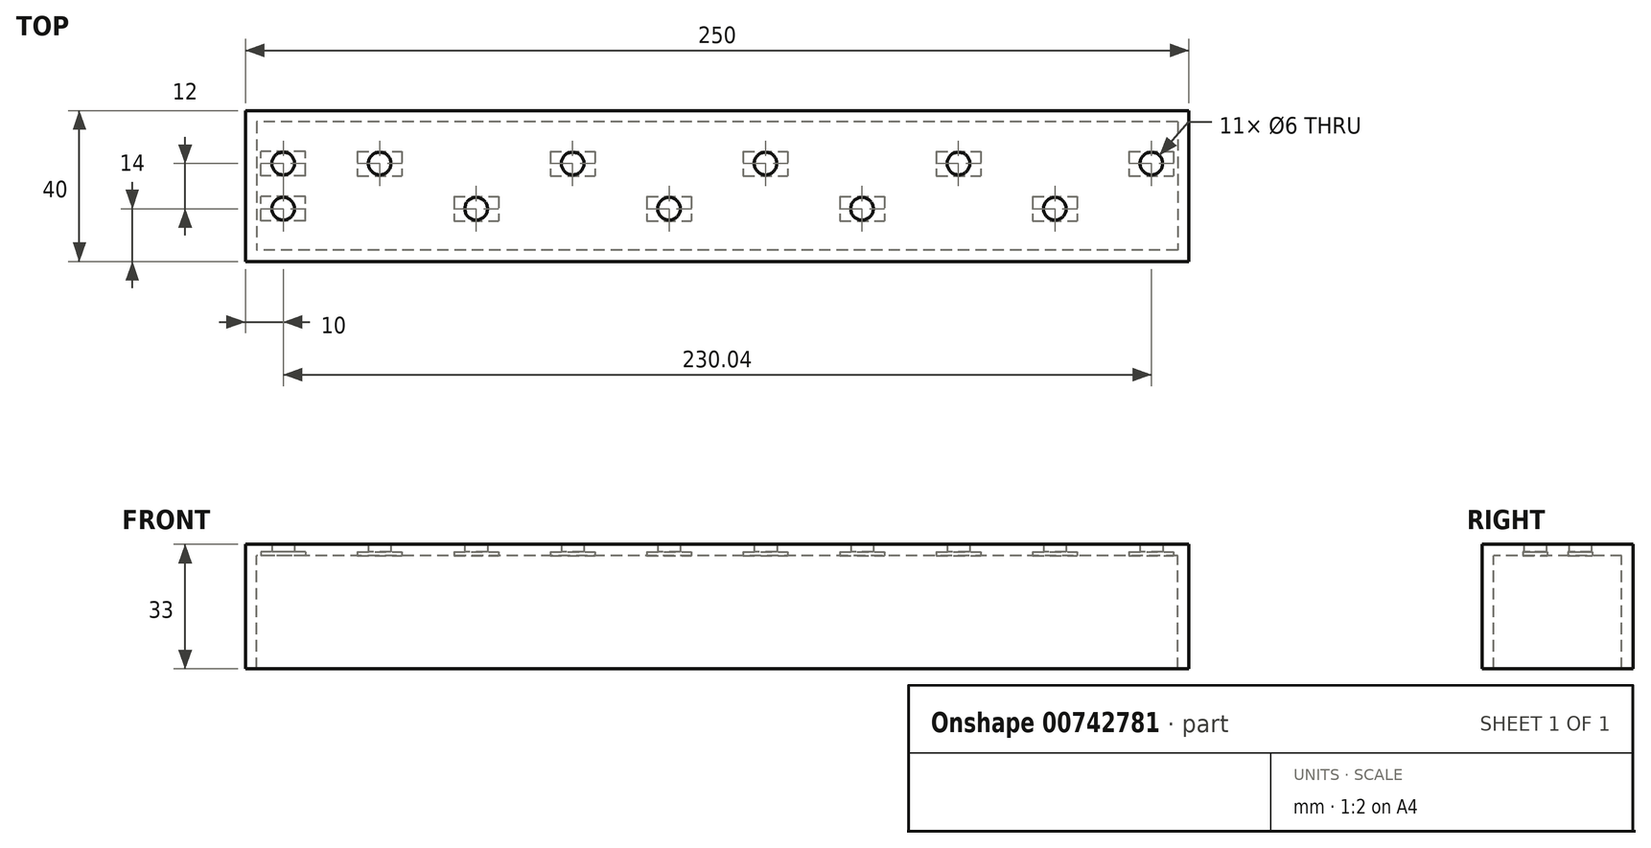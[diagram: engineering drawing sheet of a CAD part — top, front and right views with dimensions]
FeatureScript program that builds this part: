
annotation { "Feature Type Name" : "Feature", "Feature Type Description" : "" }
export const myFeature = defineFeature(function(context is Context, id is Id, definition is map)
    precondition{}
    {
        {
            var Q0;
            Q0=qCreatedBy(makeId("Top.planeOp"),FACE);
            var sketch = newSketch(context, id + "F0", { "sketchPlane" : qUnion([Q0])});
            skLineSegment(sketch, "E0.bottom", {"start": v(125, 20) * mm, "end": v(-125, 20) * mm});
            skLineSegment(sketch, "E0.top", {"start": v(125, -20) * mm, "end": v(-125, -20) * mm});
            skLineSegment(sketch, "E0.left", {"start": v(125, 20) * mm, "end": v(125, -20) * mm});
            skLineSegment(sketch, "E0.right", {"start": v(-125, 20) * mm, "end": v(-125, -20) * mm});
            skPoint(sketch, "E0.middle", {"position": v(0, 0) * mm});
            skLineSegment(sketch, "E1.bottom", {"start": v(115, 6) * mm, "end": v(-115, 6) * mm});
            skLineSegment(sketch, "E1.top", {"start": v(115, -6) * mm, "end": v(-115, -6) * mm});
            skLineSegment(sketch, "E1.left", {"start": v(115, 6) * mm, "end": v(115, -6) * mm});
            skLineSegment(sketch, "E1.right", {"start": v(-115, 6) * mm, "end": v(-115, -6) * mm});
            skCircle(sketch, "E2", {"center": v(-115, -6) * mm, "radius": 3 * mm});
            skLineSegment(sketch, "E3.bottom", {"start": v(-109.1, -9.25) * mm, "end": v(-109.1, -2.75) * mm});
            skLineSegment(sketch, "E3.top", {"start": v(-120.9, -9.25) * mm, "end": v(-120.9, -2.75) * mm});
            skLineSegment(sketch, "E3.left", {"start": v(-109.1, -9.25) * mm, "end": v(-120.9, -9.25) * mm});
            skLineSegment(sketch, "E3.right", {"start": v(-109.1, -2.75) * mm, "end": v(-120.9, -2.75) * mm});
            skCircle(sketch, "E4.0.1.0", {"center": v(-115, 6) * mm, "radius": 3 * mm});
            skPoint(sketch, "E4.0.1.1", {"position": v(-115, 6) * mm});
            skLineSegment(sketch, "E4.0.1.2", {"start": v(-109.1, 2.75) * mm, "end": v(-109.1, 9.25) * mm});
            skLineSegment(sketch, "E4.0.1.3", {"start": v(-120.9, 2.75) * mm, "end": v(-120.9, 9.25) * mm});
            skLineSegment(sketch, "E4.0.1.4", {"start": v(-109.1, 2.75) * mm, "end": v(-120.9, 2.75) * mm});
            skLineSegment(sketch, "E4.0.1.5", {"start": v(-109.1, 9.25) * mm, "end": v(-120.9, 9.25) * mm});
            skCircle(sketch, "E4.1.1.0", {"center": v(-89.44, 6) * mm, "radius": 3 * mm});
            skPoint(sketch, "E4.1.1.1", {"position": v(-89.44, 6) * mm});
            skLineSegment(sketch, "E4.1.1.2", {"start": v(-95.34, 9.25) * mm, "end": v(-95.34, 2.75) * mm});
            skLineSegment(sketch, "E4.1.1.3", {"start": v(-83.54, 9.25) * mm, "end": v(-83.54, 2.75) * mm});
            skLineSegment(sketch, "E4.1.1.4", {"start": v(-95.34, 9.25) * mm, "end": v(-83.54, 9.25) * mm});
            skLineSegment(sketch, "E4.1.1.5", {"start": v(-95.34, 2.75) * mm, "end": v(-83.54, 2.75) * mm});
            skCircle(sketch, "E4.2.0.0", {"center": v(-63.88, -6) * mm, "radius": 3 * mm});
            skPoint(sketch, "E4.2.0.1", {"position": v(-63.88, -6) * mm});
            skLineSegment(sketch, "E4.2.0.2", {"start": v(-69.78, -2.75) * mm, "end": v(-69.78, -9.25) * mm});
            skLineSegment(sketch, "E4.2.0.3", {"start": v(-57.98, -2.75) * mm, "end": v(-57.98, -9.25) * mm});
            skLineSegment(sketch, "E4.2.0.4", {"start": v(-69.78, -2.75) * mm, "end": v(-57.98, -2.75) * mm});
            skLineSegment(sketch, "E4.2.0.5", {"start": v(-69.78, -9.25) * mm, "end": v(-57.98, -9.25) * mm});
            skCircle(sketch, "E4.3.1.0", {"center": v(-38.32, 6) * mm, "radius": 3 * mm});
            skPoint(sketch, "E4.3.1.1", {"position": v(-38.32, 6) * mm});
            skLineSegment(sketch, "E4.3.1.2", {"start": v(-44.22, 9.25) * mm, "end": v(-44.22, 2.75) * mm});
            skLineSegment(sketch, "E4.3.1.3", {"start": v(-32.42, 9.25) * mm, "end": v(-32.42, 2.75) * mm});
            skLineSegment(sketch, "E4.3.1.4", {"start": v(-44.22, 9.25) * mm, "end": v(-32.42, 9.25) * mm});
            skLineSegment(sketch, "E4.3.1.5", {"start": v(-44.22, 2.75) * mm, "end": v(-32.42, 2.75) * mm});
            skCircle(sketch, "E4.4.0.0", {"center": v(-12.76, -6) * mm, "radius": 3 * mm});
            skPoint(sketch, "E4.4.0.1", {"position": v(-12.76, -6) * mm});
            skLineSegment(sketch, "E4.4.0.2", {"start": v(-18.66, -2.75) * mm, "end": v(-18.66, -9.25) * mm});
            skLineSegment(sketch, "E4.4.0.3", {"start": v(-6.86, -2.75) * mm, "end": v(-6.86, -9.25) * mm});
            skLineSegment(sketch, "E4.4.0.4", {"start": v(-18.66, -2.75) * mm, "end": v(-6.86, -2.75) * mm});
            skLineSegment(sketch, "E4.4.0.5", {"start": v(-18.66, -9.25) * mm, "end": v(-6.86, -9.25) * mm});
            skCircle(sketch, "E4.5.1.0", {"center": v(12.8, 6) * mm, "radius": 3 * mm});
            skPoint(sketch, "E4.5.1.1", {"position": v(12.8, 6) * mm});
            skLineSegment(sketch, "E4.5.1.2", {"start": v(6.9, 9.25) * mm, "end": v(6.9, 2.75) * mm});
            skLineSegment(sketch, "E4.5.1.3", {"start": v(18.7, 9.25) * mm, "end": v(18.7, 2.75) * mm});
            skLineSegment(sketch, "E4.5.1.4", {"start": v(6.9, 9.25) * mm, "end": v(18.7, 9.25) * mm});
            skLineSegment(sketch, "E4.5.1.5", {"start": v(6.9, 2.75) * mm, "end": v(18.7, 2.75) * mm});
            skCircle(sketch, "E4.6.0.0", {"center": v(38.36, -6) * mm, "radius": 3 * mm});
            skPoint(sketch, "E4.6.0.1", {"position": v(38.36, -6) * mm});
            skLineSegment(sketch, "E4.6.0.2", {"start": v(32.46, -2.75) * mm, "end": v(32.46, -9.25) * mm});
            skLineSegment(sketch, "E4.6.0.3", {"start": v(44.26, -2.75) * mm, "end": v(44.26, -9.25) * mm});
            skLineSegment(sketch, "E4.6.0.4", {"start": v(32.46, -2.75) * mm, "end": v(44.26, -2.75) * mm});
            skLineSegment(sketch, "E4.6.0.5", {"start": v(32.46, -9.25) * mm, "end": v(44.26, -9.25) * mm});
            skCircle(sketch, "E4.7.1.0", {"center": v(63.92, 6) * mm, "radius": 3 * mm});
            skPoint(sketch, "E4.7.1.1", {"position": v(63.92, 6) * mm});
            skLineSegment(sketch, "E4.7.1.2", {"start": v(58.02, 9.25) * mm, "end": v(58.02, 2.75) * mm});
            skLineSegment(sketch, "E4.7.1.3", {"start": v(69.82, 9.25) * mm, "end": v(69.82, 2.75) * mm});
            skLineSegment(sketch, "E4.7.1.4", {"start": v(58.02, 9.25) * mm, "end": v(69.82, 9.25) * mm});
            skLineSegment(sketch, "E4.7.1.5", {"start": v(58.02, 2.75) * mm, "end": v(69.82, 2.75) * mm});
            skCircle(sketch, "E4.8.0.0", {"center": v(89.48, -6) * mm, "radius": 3 * mm});
            skPoint(sketch, "E4.8.0.1", {"position": v(89.48, -6) * mm});
            skLineSegment(sketch, "E4.8.0.2", {"start": v(83.58, -2.75) * mm, "end": v(83.58, -9.25) * mm});
            skLineSegment(sketch, "E4.8.0.3", {"start": v(95.38, -2.75) * mm, "end": v(95.38, -9.25) * mm});
            skLineSegment(sketch, "E4.8.0.4", {"start": v(83.58, -2.75) * mm, "end": v(95.38, -2.75) * mm});
            skLineSegment(sketch, "E4.8.0.5", {"start": v(83.58, -9.25) * mm, "end": v(95.38, -9.25) * mm});
            skCircle(sketch, "E4.9.1.0", {"center": v(115.04, 6) * mm, "radius": 3 * mm});
            skPoint(sketch, "E4.9.1.1", {"position": v(115.04, 6) * mm});
            skLineSegment(sketch, "E4.9.1.2", {"start": v(109.14, 9.25) * mm, "end": v(109.14, 2.75) * mm});
            skLineSegment(sketch, "E4.9.1.3", {"start": v(120.94, 9.25) * mm, "end": v(120.94, 2.75) * mm});
            skLineSegment(sketch, "E4.9.1.4", {"start": v(109.14, 9.25) * mm, "end": v(120.94, 9.25) * mm});
            skLineSegment(sketch, "E4.9.1.5", {"start": v(109.14, 2.75) * mm, "end": v(120.94, 2.75) * mm});
            skLineSegment(sketch, "E4.direction1", {"start": v(-118.25, -11.9) * mm, "end": v(-92.7, -11.9) * mm, "construction": true});
            skLineSegment(sketch, "E4.direction2", {"start": v(-120.9, -2.75) * mm, "end": v(-108.9, -2.75) * mm, "construction": true});
            skLineSegment(sketch, "E5.0", {"start": v(122, 17) * mm, "end": v(-122, 17) * mm});
            skLineSegment(sketch, "E5.1", {"start": v(122, 17) * mm, "end": v(122, -17) * mm});
            skLineSegment(sketch, "E5.2", {"start": v(122, -17) * mm, "end": v(-122, -17) * mm});
            skLineSegment(sketch, "E5.3", {"start": v(-122, 17) * mm, "end": v(-122, -17) * mm});
            skSolve(sketch);
        }
        {
            var Q0;
            Q0=makeQuery(id+"F0.imprint","IMPRINT",FACE,{"disambiguationData":[TD([[makeQuery(id+"F0.imprint","IMPRINT",EDGE,{"derivedFrom":sQuery(id+"F0.wireOp",EDGE,"E0.bottom")}),1.0]])]});
            var Q1;
            {var subQ0=sQuery(id+"F0.wireOp",EDGE,"E4.4.0.5");Q1=makeQuery(id+"F0.imprint","IMPRINT",FACE,{"disambiguationData":[TD([[makeQuery(id+"F0.imprint","IMPRINT",EDGE,{"derivedFrom":subQ0}),1.0]])]});}
            var Q2;
            {var subQ6=sQuery(id+"F0.wireOp",EDGE,"E4.4.0.4");Q2=makeQuery(id+"F0.imprint","IMPRINT",FACE,{"disambiguationData":[TD([[makeQuery(id+"F0.imprint","IMPRINT",EDGE,{"derivedFrom":subQ6}),-1.0]])]});}
            var Q3;
            {var subQ0=sQuery(id+"F0.wireOp",EDGE,"E4.9.1.0");var subQ1=sQuery(id+"F0.wireOp",EDGE,"E1.bottom");var subQ2=makeQuery(id+"F0.imprint","INTERSECT",VERTEX,{"derivedFrom":[subQ1,subQ0]});Q3=makeQuery(id+"F0.imprint","IMPRINT",FACE,{"disambiguationData":[TD([[makeQuery(id+"F0.imprint","IMPRINT",EDGE,{"disambiguationData":[TD([[subQ2,-1.0]])],"derivedFrom":subQ1}),1.0]])]});}
            var Q4;
            {var subQ0=sQuery(id+"F0.wireOp",EDGE,"E4.6.0.5");Q4=makeQuery(id+"F0.imprint","IMPRINT",FACE,{"disambiguationData":[TD([[makeQuery(id+"F0.imprint","IMPRINT",EDGE,{"derivedFrom":subQ0}),1.0]])]});}
            var Q5;
            {var subQ6=sQuery(id+"F0.wireOp",EDGE,"E4.6.0.4");Q5=makeQuery(id+"F0.imprint","IMPRINT",FACE,{"disambiguationData":[TD([[makeQuery(id+"F0.imprint","IMPRINT",EDGE,{"derivedFrom":subQ6}),-1.0]])]});}
            var Q6;
            {var subQ4=sQuery(id+"F0.wireOp",EDGE,"E4.1.1.5");Q6=makeQuery(id+"F0.imprint","IMPRINT",FACE,{"disambiguationData":[TD([[makeQuery(id+"F0.imprint","IMPRINT",EDGE,{"derivedFrom":subQ4}),1.0]])]});}
            var Q7;
            {var subQ0=sQuery(id+"F0.wireOp",EDGE,"E4.1.1.4");Q7=makeQuery(id+"F0.imprint","IMPRINT",FACE,{"disambiguationData":[TD([[makeQuery(id+"F0.imprint","IMPRINT",EDGE,{"derivedFrom":subQ0}),-1.0]])]});}
            var Q8;
            {var subQ4=sQuery(id+"F0.wireOp",EDGE,"E4.7.1.5");Q8=makeQuery(id+"F0.imprint","IMPRINT",FACE,{"disambiguationData":[TD([[makeQuery(id+"F0.imprint","IMPRINT",EDGE,{"derivedFrom":subQ4}),1.0]])]});}
            var Q9;
            {var subQ0=sQuery(id+"F0.wireOp",EDGE,"E4.7.1.4");Q9=makeQuery(id+"F0.imprint","IMPRINT",FACE,{"disambiguationData":[TD([[makeQuery(id+"F0.imprint","IMPRINT",EDGE,{"derivedFrom":subQ0}),-1.0]])]});}
            var Q10;
            {var subQ0=sQuery(id+"F0.wireOp",EDGE,"E4.8.0.5");Q10=makeQuery(id+"F0.imprint","IMPRINT",FACE,{"disambiguationData":[TD([[makeQuery(id+"F0.imprint","IMPRINT",EDGE,{"derivedFrom":subQ0}),1.0]])]});}
            var Q11;
            {var subQ8=sQuery(id+"F0.wireOp",EDGE,"E4.8.0.4");Q11=makeQuery(id+"F0.imprint","IMPRINT",FACE,{"disambiguationData":[TD([[makeQuery(id+"F0.imprint","IMPRINT",EDGE,{"derivedFrom":subQ8}),-1.0]])]});}
            var Q12;
            {var subQ8=sQuery(id+"F0.wireOp",EDGE,"E4.1.1.5");Q12=makeQuery(id+"F0.imprint","IMPRINT",FACE,{"disambiguationData":[TD([[makeQuery(id+"F0.imprint","IMPRINT",EDGE,{"derivedFrom":subQ8}),-1.0]])]});}
            var Q13;
            {var subQ4=sQuery(id+"F0.wireOp",EDGE,"E4.5.1.5");Q13=makeQuery(id+"F0.imprint","IMPRINT",FACE,{"disambiguationData":[TD([[makeQuery(id+"F0.imprint","IMPRINT",EDGE,{"derivedFrom":subQ4}),1.0]])]});}
            var Q14;
            {var subQ0=sQuery(id+"F0.wireOp",EDGE,"E4.5.1.4");Q14=makeQuery(id+"F0.imprint","IMPRINT",FACE,{"disambiguationData":[TD([[makeQuery(id+"F0.imprint","IMPRINT",EDGE,{"derivedFrom":subQ0}),-1.0]])]});}
            var Q15;
            {var subQ4=sQuery(id+"F0.wireOp",EDGE,"E4.3.1.5");Q15=makeQuery(id+"F0.imprint","IMPRINT",FACE,{"disambiguationData":[TD([[makeQuery(id+"F0.imprint","IMPRINT",EDGE,{"derivedFrom":subQ4}),1.0]])]});}
            var Q16;
            {var subQ0=sQuery(id+"F0.wireOp",EDGE,"E4.3.1.4");Q16=makeQuery(id+"F0.imprint","IMPRINT",FACE,{"disambiguationData":[TD([[makeQuery(id+"F0.imprint","IMPRINT",EDGE,{"derivedFrom":subQ0}),-1.0]])]});}
            var Q17;
            {var subQ45=sQuery(id+"F0.wireOp",EDGE,"E3.top");Q17=makeQuery(id+"F0.imprint","IMPRINT",FACE,{"disambiguationData":[TD([[makeQuery(id+"F0.imprint","IMPRINT",EDGE,{"derivedFrom":subQ45}),1.0]])]});}
            var Q18;
            {var subQ0=sQuery(id+"F0.wireOp",EDGE,"E4.2.0.5");Q18=makeQuery(id+"F0.imprint","IMPRINT",FACE,{"disambiguationData":[TD([[makeQuery(id+"F0.imprint","IMPRINT",EDGE,{"derivedFrom":subQ0}),1.0]])]});}
            var Q19;
            {var subQ6=sQuery(id+"F0.wireOp",EDGE,"E4.2.0.4");Q19=makeQuery(id+"F0.imprint","IMPRINT",FACE,{"disambiguationData":[TD([[makeQuery(id+"F0.imprint","IMPRINT",EDGE,{"derivedFrom":subQ6}),-1.0]])]});}
            var Q20;
            {var subQ10=sQuery(id+"F0.wireOp",EDGE,"E4.9.1.3");Q20=makeQuery(id+"F0.imprint","IMPRINT",FACE,{"disambiguationData":[TD([[makeQuery(id+"F0.imprint","IMPRINT",EDGE,{"derivedFrom":subQ10}),-1.0]])]});}
            var Q21;
            {var subQ10=sQuery(id+"F0.wireOp",EDGE,"E3.top");Q21=makeQuery(id+"F0.imprint","IMPRINT",FACE,{"disambiguationData":[TD([[makeQuery(id+"F0.imprint","IMPRINT",EDGE,{"derivedFrom":subQ10}),-1.0]])]});}
            var Q22;
            {var subQ1=sQuery(id+"F0.wireOp",EDGE,"E3.bottom");var subQ3=sQuery(id+"F0.wireOp",EDGE,"E1.top");var subQ4=makeQuery(id+"F0.imprint","INTERSECT",VERTEX,{"derivedFrom":[subQ3,subQ1]});Q22=makeQuery(id+"F0.imprint","IMPRINT",FACE,{"disambiguationData":[TD([[makeQuery(id+"F0.imprint","IMPRINT",EDGE,{"disambiguationData":[TD([[subQ4,-1.0]])],"derivedFrom":subQ3}),-1.0]])]});}
            var Q23;
            {var subQ1=sQuery(id+"F0.wireOp",EDGE,"E4.0.1.2");var subQ3=sQuery(id+"F0.wireOp",EDGE,"E1.bottom");var subQ4=makeQuery(id+"F0.imprint","INTERSECT",VERTEX,{"derivedFrom":[subQ3,subQ1]});Q23=makeQuery(id+"F0.imprint","IMPRINT",FACE,{"disambiguationData":[TD([[makeQuery(id+"F0.imprint","IMPRINT",EDGE,{"disambiguationData":[TD([[subQ4,-1.0]])],"derivedFrom":subQ3}),1.0]])]});}
            var Q24;
            {var subQ10=sQuery(id+"F0.wireOp",EDGE,"E4.0.1.3");Q24=makeQuery(id+"F0.imprint","IMPRINT",FACE,{"disambiguationData":[TD([[makeQuery(id+"F0.imprint","IMPRINT",EDGE,{"derivedFrom":subQ10}),-1.0]])]});}
            extrude(context, id + "F1", {"entities" : qUnion([Q0, Q1, Q2, Q3, Q4, Q5, Q6, Q7, Q8, Q9, Q10, Q11, Q12, Q13, Q14, Q15, Q16, Q17, Q18, Q19, Q20, Q21, Q22, Q23, Q24]), "depth" : 3 * mm, "offsetDistance" : 25 * mm});
        }
        {
            var Q0;
            {var subQ4=sQuery(id+"F0.wireOp",EDGE,"E4.7.1.5");Q0=makeQuery(id+"F0.imprint","IMPRINT",FACE,{"disambiguationData":[TD([[makeQuery(id+"F0.imprint","IMPRINT",EDGE,{"derivedFrom":subQ4}),1.0]])]});}
            var Q1;
            {var subQ0=sQuery(id+"F0.wireOp",EDGE,"E4.7.1.4");Q1=makeQuery(id+"F0.imprint","IMPRINT",FACE,{"disambiguationData":[TD([[makeQuery(id+"F0.imprint","IMPRINT",EDGE,{"derivedFrom":subQ0}),-1.0]])]});}
            var Q2;
            {var subQ0=sQuery(id+"F0.wireOp",EDGE,"E4.6.0.5");Q2=makeQuery(id+"F0.imprint","IMPRINT",FACE,{"disambiguationData":[TD([[makeQuery(id+"F0.imprint","IMPRINT",EDGE,{"derivedFrom":subQ0}),1.0]])]});}
            var Q3;
            {var subQ6=sQuery(id+"F0.wireOp",EDGE,"E4.6.0.4");Q3=makeQuery(id+"F0.imprint","IMPRINT",FACE,{"disambiguationData":[TD([[makeQuery(id+"F0.imprint","IMPRINT",EDGE,{"derivedFrom":subQ6}),-1.0]])]});}
            var Q4;
            {var subQ4=sQuery(id+"F0.wireOp",EDGE,"E4.5.1.5");Q4=makeQuery(id+"F0.imprint","IMPRINT",FACE,{"disambiguationData":[TD([[makeQuery(id+"F0.imprint","IMPRINT",EDGE,{"derivedFrom":subQ4}),1.0]])]});}
            var Q5;
            {var subQ0=sQuery(id+"F0.wireOp",EDGE,"E4.5.1.4");Q5=makeQuery(id+"F0.imprint","IMPRINT",FACE,{"disambiguationData":[TD([[makeQuery(id+"F0.imprint","IMPRINT",EDGE,{"derivedFrom":subQ0}),-1.0]])]});}
            var Q6;
            {var subQ0=sQuery(id+"F0.wireOp",EDGE,"E4.4.0.5");Q6=makeQuery(id+"F0.imprint","IMPRINT",FACE,{"disambiguationData":[TD([[makeQuery(id+"F0.imprint","IMPRINT",EDGE,{"derivedFrom":subQ0}),1.0]])]});}
            var Q7;
            {var subQ6=sQuery(id+"F0.wireOp",EDGE,"E4.4.0.4");Q7=makeQuery(id+"F0.imprint","IMPRINT",FACE,{"disambiguationData":[TD([[makeQuery(id+"F0.imprint","IMPRINT",EDGE,{"derivedFrom":subQ6}),-1.0]])]});}
            var Q8;
            {var subQ8=sQuery(id+"F0.wireOp",EDGE,"E4.8.0.4");Q8=makeQuery(id+"F0.imprint","IMPRINT",FACE,{"disambiguationData":[TD([[makeQuery(id+"F0.imprint","IMPRINT",EDGE,{"derivedFrom":subQ8}),-1.0]])]});}
            var Q9;
            {var subQ0=sQuery(id+"F0.wireOp",EDGE,"E4.9.1.0");var subQ1=sQuery(id+"F0.wireOp",EDGE,"E1.bottom");var subQ2=makeQuery(id+"F0.imprint","INTERSECT",VERTEX,{"derivedFrom":[subQ1,subQ0]});Q9=makeQuery(id+"F0.imprint","IMPRINT",FACE,{"disambiguationData":[TD([[makeQuery(id+"F0.imprint","IMPRINT",EDGE,{"disambiguationData":[TD([[subQ2,-1.0]])],"derivedFrom":subQ1}),1.0]])]});}
            var Q10;
            {var subQ4=sQuery(id+"F0.wireOp",EDGE,"E4.3.1.5");Q10=makeQuery(id+"F0.imprint","IMPRINT",FACE,{"disambiguationData":[TD([[makeQuery(id+"F0.imprint","IMPRINT",EDGE,{"derivedFrom":subQ4}),1.0]])]});}
            var Q11;
            {var subQ0=sQuery(id+"F0.wireOp",EDGE,"E4.3.1.4");Q11=makeQuery(id+"F0.imprint","IMPRINT",FACE,{"disambiguationData":[TD([[makeQuery(id+"F0.imprint","IMPRINT",EDGE,{"derivedFrom":subQ0}),-1.0]])]});}
            var Q12;
            {var subQ0=sQuery(id+"F0.wireOp",EDGE,"E4.2.0.5");Q12=makeQuery(id+"F0.imprint","IMPRINT",FACE,{"disambiguationData":[TD([[makeQuery(id+"F0.imprint","IMPRINT",EDGE,{"derivedFrom":subQ0}),1.0]])]});}
            var Q13;
            {var subQ6=sQuery(id+"F0.wireOp",EDGE,"E4.2.0.4");Q13=makeQuery(id+"F0.imprint","IMPRINT",FACE,{"disambiguationData":[TD([[makeQuery(id+"F0.imprint","IMPRINT",EDGE,{"derivedFrom":subQ6}),-1.0]])]});}
            var Q14;
            {var subQ4=sQuery(id+"F0.wireOp",EDGE,"E4.1.1.5");Q14=makeQuery(id+"F0.imprint","IMPRINT",FACE,{"disambiguationData":[TD([[makeQuery(id+"F0.imprint","IMPRINT",EDGE,{"derivedFrom":subQ4}),1.0]])]});}
            var Q15;
            {var subQ0=sQuery(id+"F0.wireOp",EDGE,"E4.1.1.4");Q15=makeQuery(id+"F0.imprint","IMPRINT",FACE,{"disambiguationData":[TD([[makeQuery(id+"F0.imprint","IMPRINT",EDGE,{"derivedFrom":subQ0}),-1.0]])]});}
            var Q16;
            {var subQ1=sQuery(id+"F0.wireOp",EDGE,"E4.0.1.2");var subQ3=sQuery(id+"F0.wireOp",EDGE,"E1.bottom");var subQ4=makeQuery(id+"F0.imprint","INTERSECT",VERTEX,{"derivedFrom":[subQ3,subQ1]});Q16=makeQuery(id+"F0.imprint","IMPRINT",FACE,{"disambiguationData":[TD([[makeQuery(id+"F0.imprint","IMPRINT",EDGE,{"disambiguationData":[TD([[subQ4,-1.0]])],"derivedFrom":subQ3}),1.0]])]});}
            var Q17;
            {var subQ10=sQuery(id+"F0.wireOp",EDGE,"E3.top");Q17=makeQuery(id+"F0.imprint","IMPRINT",FACE,{"disambiguationData":[TD([[makeQuery(id+"F0.imprint","IMPRINT",EDGE,{"derivedFrom":subQ10}),-1.0]])]});}
            var Q18;
            {var subQ10=sQuery(id+"F0.wireOp",EDGE,"E4.9.1.3");Q18=makeQuery(id+"F0.imprint","IMPRINT",FACE,{"disambiguationData":[TD([[makeQuery(id+"F0.imprint","IMPRINT",EDGE,{"derivedFrom":subQ10}),-1.0]])]});}
            var Q19;
            {var subQ0=sQuery(id+"F0.wireOp",EDGE,"E4.8.0.5");Q19=makeQuery(id+"F0.imprint","IMPRINT",FACE,{"disambiguationData":[TD([[makeQuery(id+"F0.imprint","IMPRINT",EDGE,{"derivedFrom":subQ0}),1.0]])]});}
            var Q20;
            {var subQ10=sQuery(id+"F0.wireOp",EDGE,"E4.0.1.3");Q20=makeQuery(id+"F0.imprint","IMPRINT",FACE,{"disambiguationData":[TD([[makeQuery(id+"F0.imprint","IMPRINT",EDGE,{"derivedFrom":subQ10}),-1.0]])]});}
            var Q21;
            {var subQ1=sQuery(id+"F0.wireOp",EDGE,"E3.bottom");var subQ3=sQuery(id+"F0.wireOp",EDGE,"E1.top");var subQ4=makeQuery(id+"F0.imprint","INTERSECT",VERTEX,{"derivedFrom":[subQ3,subQ1]});Q21=makeQuery(id+"F0.imprint","IMPRINT",FACE,{"disambiguationData":[TD([[makeQuery(id+"F0.imprint","IMPRINT",EDGE,{"disambiguationData":[TD([[subQ4,-1.0]])],"derivedFrom":subQ3}),-1.0]])]});}
            extrude(context, id + "F2", {"entities" : qUnion([Q0, Q1, Q2, Q3, Q4, Q5, Q6, Q7, Q8, Q9, Q10, Q11, Q12, Q13, Q14, Q15, Q16, Q17, Q18, Q19, Q20, Q21]), "operationType" : NewBodyOperationType.REMOVE, "depth" : 1 * mm, "offsetDistance" : 25 * mm});
        }
        {
            var Q0;
            Q0=makeQuery(id+"F0.imprint","IMPRINT",FACE,{"disambiguationData":[TD([[makeQuery(id+"F0.imprint","IMPRINT",EDGE,{"derivedFrom":sQuery(id+"F0.wireOp",EDGE,"E0.bottom")}),1.0]])]});
            extrude(context, id + "F3", {"entities" : qUnion([Q0]), "operationType" : NewBodyOperationType.ADD, "oppositeDirection" : true, "depth" : 30 * mm, "offsetDistance" : 25 * mm});
        }
    });
